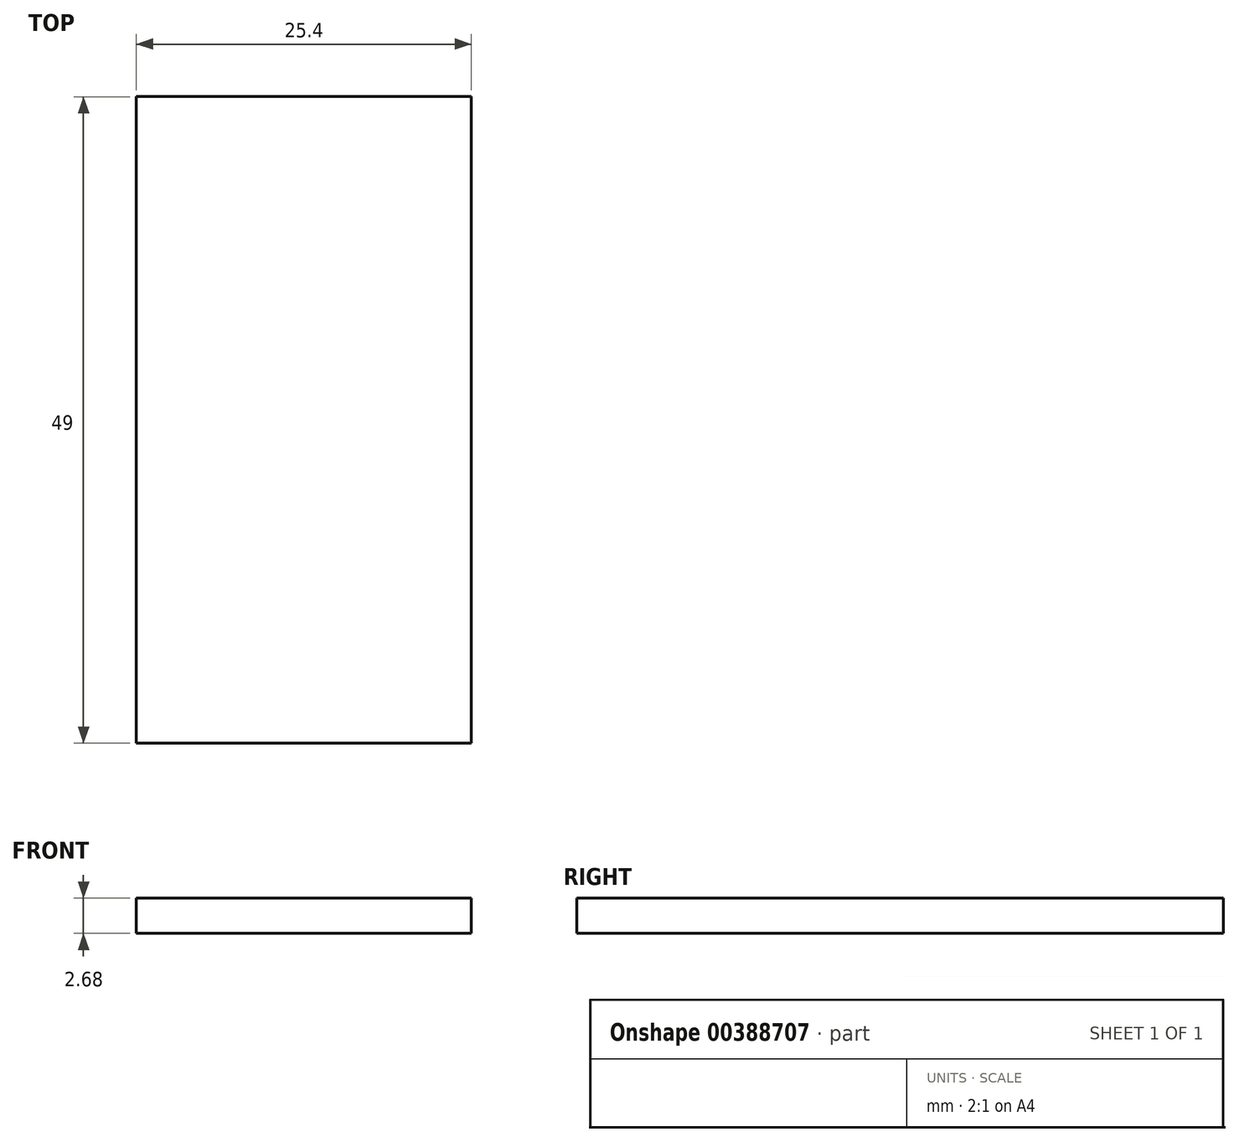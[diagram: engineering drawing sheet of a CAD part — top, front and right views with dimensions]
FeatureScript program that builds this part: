
annotation { "Feature Type Name" : "Feature", "Feature Type Description" : "" }
export const myFeature = defineFeature(function(context is Context, id is Id, definition is map)
    precondition{}
    {
        {
            var Q0;
            Q0=qCreatedBy(makeId("Right.planeOp"),FACE);
            var sketch = newSketch(context, id + "F0", { "sketchPlane" : qUnion([Q0])});
            skLineSegment(sketch, "E0.bottom", {"start": v(-39.9, 23.03) * mm, "end": v(9.1, 23.03) * mm});
            skLineSegment(sketch, "E0.top", {"start": v(-39.9, 20.35) * mm, "end": v(9.1, 20.35) * mm});
            skLineSegment(sketch, "E0.left", {"start": v(-39.9, 23.03) * mm, "end": v(-39.9, 20.35) * mm});
            skLineSegment(sketch, "E0.right", {"start": v(9.1, 23.03) * mm, "end": v(9.1, 20.35) * mm});
            skLineSegment(sketch, "E1.bottom", {"start": v(-47.68, 25.43) * mm, "end": v(-38.79, 25.43) * mm});
            skLineSegment(sketch, "E1.top", {"start": v(-47.68, 23.03) * mm, "end": v(-38.79, 23.03) * mm});
            skLineSegment(sketch, "E1.left", {"start": v(-47.68, 25.43) * mm, "end": v(-47.68, 23.03) * mm});
            skLineSegment(sketch, "E1.right", {"start": v(-38.79, 25.43) * mm, "end": v(-38.79, 23.03) * mm});
            skLineSegment(sketch, "E2.bottom", {"start": v(9.1, 26.99) * mm, "end": v(16.72, 26.99) * mm});
            skLineSegment(sketch, "E2.top", {"start": v(9.1, 18.23) * mm, "end": v(16.72, 18.23) * mm});
            skLineSegment(sketch, "E2.left", {"start": v(9.1, 26.99) * mm, "end": v(9.1, 18.23) * mm});
            skLineSegment(sketch, "E2.right", {"start": v(16.72, 26.99) * mm, "end": v(16.72, 18.23) * mm});
            skPoint(sketch, "E3.firstSnap0", {"position": v(16.72, 22.6) * mm});
            skLineSegment(sketch, "E3.bottom", {"start": v(19.7, 22.6) * mm, "end": v(27.31, 22.6) * mm});
            skLineSegment(sketch, "E3.top", {"start": v(19.7, 20.53) * mm, "end": v(27.31, 20.53) * mm});
            skLineSegment(sketch, "E3.left", {"start": v(19.7, 22.6) * mm, "end": v(19.7, 20.53) * mm});
            skLineSegment(sketch, "E3.right", {"start": v(27.31, 22.6) * mm, "end": v(27.31, 20.53) * mm});
            skSolve(sketch);
        }
        {
            var Q0;
            {var subQ1=sQuery(id+"F0.wireOp",EDGE,"E0.bottom");Q0=makeQuery(id+"F0.imprint","IMPRINT",FACE,{"disambiguationData":[TD([[makeQuery(id+"F0.imprint","IMPRINT",EDGE,{"derivedFrom":subQ1}),-1.0]])]});}
            extrude(context, id + "F1", {"entities" : qUnion([Q0]), "endBound" : BoundingType.SYMMETRIC, "depth" : 25.4 * mm});
        }
    });
